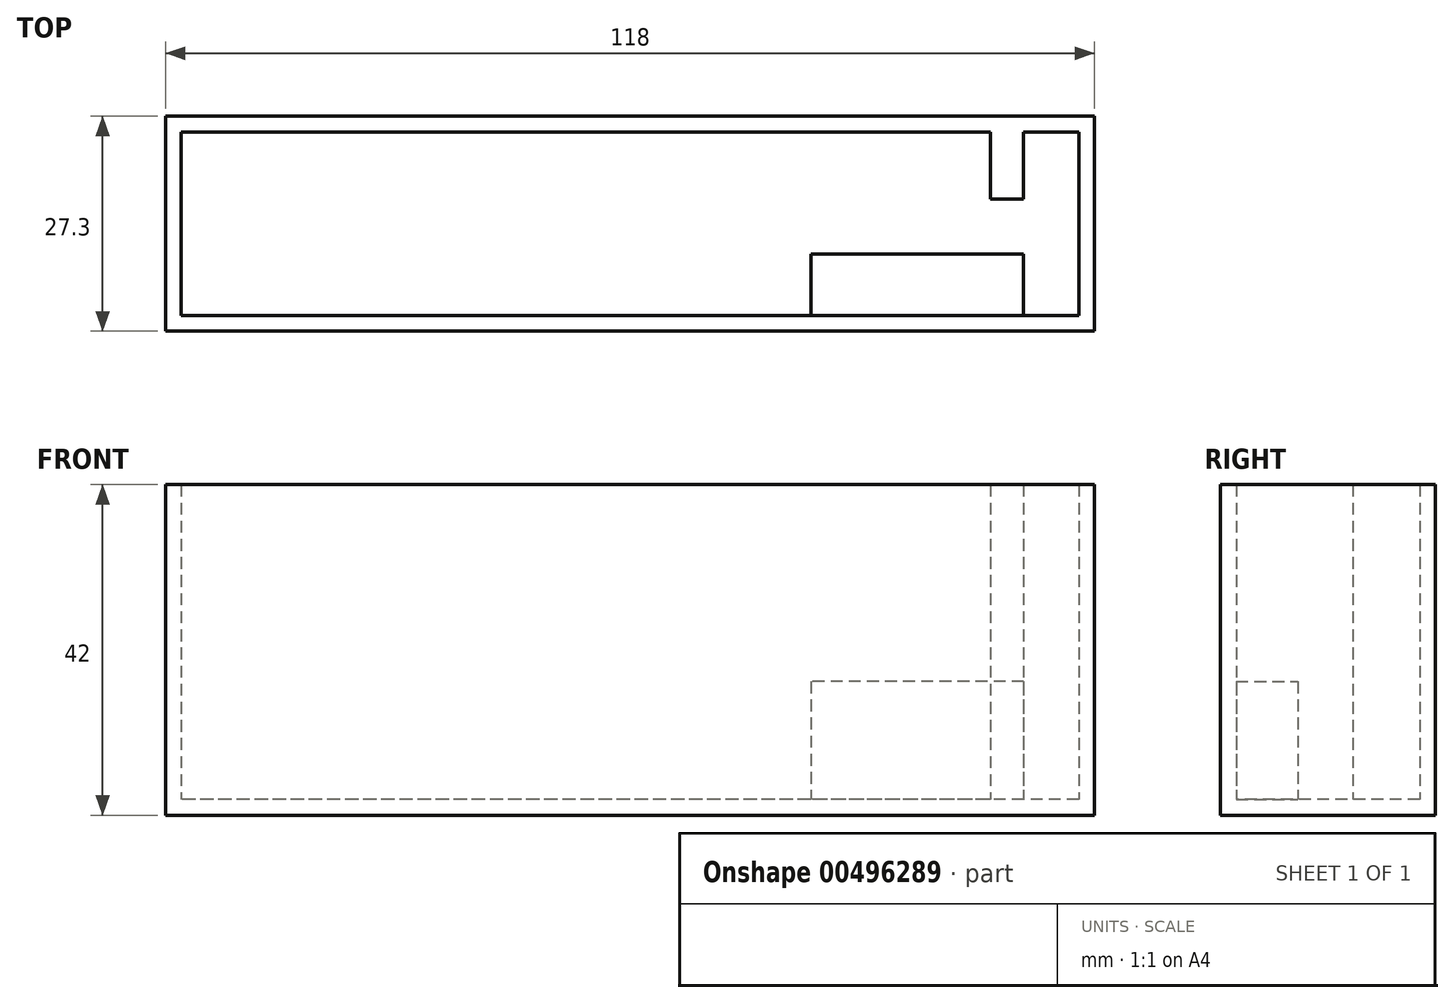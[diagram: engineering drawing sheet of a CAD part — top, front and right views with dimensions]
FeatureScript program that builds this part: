
annotation { "Feature Type Name" : "Feature", "Feature Type Description" : "" }
export const myFeature = defineFeature(function(context is Context, id is Id, definition is map)
    precondition{}
    {
        {
            var Q0;
            Q0=qCreatedBy(makeId("Top.planeOp"),FACE);
            var sketch = newSketch(context, id + "F0", { "sketchPlane" : qUnion([Q0])});
            skLineSegment(sketch, "E0.bottom", {"start": v(55.77, 11.65) * mm, "end": v(-58.23, 11.65) * mm});
            skLineSegment(sketch, "E0.top", {"start": v(55.77, -11.65) * mm, "end": v(-58.23, -11.65) * mm});
            skLineSegment(sketch, "E0.left", {"start": v(55.77, 11.65) * mm, "end": v(55.77, -11.65) * mm});
            skLineSegment(sketch, "E0.right", {"start": v(-58.23, 11.65) * mm, "end": v(-58.23, -11.65) * mm});
            skPoint(sketch, "E0.middle", {"position": v(-1.23, 0) * mm});
            skLineSegment(sketch, "E1.0", {"start": v(-60.23, 13.65) * mm, "end": v(-60.23, -13.65) * mm});
            skLineSegment(sketch, "E2.0", {"start": v(57.77, 13.65) * mm, "end": v(-60.23, 13.65) * mm});
            skLineSegment(sketch, "E3.0", {"start": v(57.77, -13.65) * mm, "end": v(-60.23, -13.65) * mm});
            skLineSegment(sketch, "E4.0", {"start": v(57.77, 13.65) * mm, "end": v(57.77, -13.65) * mm});
            skSolve(sketch);
        }
        {
            var Q0;
            Q0=qSketchRegion(id+"F0",true);
            extrude(context, id + "F1", {"entities" : qUnion([Q0]), "depth" : 40 * mm});
        }
        {
            var Q0;
            Q0=qCreatedBy(makeId("Top.planeOp"),FACE);
            var sketch = newSketch(context, id + "F2", { "sketchPlane" : qUnion([Q0])});
            skPoint(sketch, "E5.0", {"position": v(48.77, 11.65) * mm});
            skLineSegment(sketch, "E6.0", {"start": v(55.77, 11.65) * mm, "end": v(55.77, -11.65) * mm});
            skLineSegment(sketch, "E7.0", {"start": v(55.77, 11.65) * mm, "end": v(-58.23, 11.65) * mm});
            skLineSegment(sketch, "E8.0", {"start": v(55.77, -11.65) * mm, "end": v(-58.23, -11.65) * mm});
            skLineSegment(sketch, "E9", {"start": v(55.77, 11.65) * mm, "end": v(43.05, 11.65) * mm});
            skLineSegment(sketch, "E10.bottom", {"start": v(48.77, 11.65) * mm, "end": v(44.57, 11.65) * mm});
            skLineSegment(sketch, "E10.top", {"start": v(48.77, 3.15) * mm, "end": v(44.57, 3.15) * mm});
            skLineSegment(sketch, "E10.left", {"start": v(48.77, 11.65) * mm, "end": v(48.77, 3.15) * mm});
            skLineSegment(sketch, "E10.right", {"start": v(44.57, 11.65) * mm, "end": v(44.57, 3.15) * mm});
            skSolve(sketch);
        }
        {
            var Q0;
            Q0=qSketchRegion(id+"F2",true);
            extrude(context, id + "F3", {"entities" : qUnion([Q0]), "operationType" : NewBodyOperationType.ADD, "depth" : 40 * mm});
        }
        {
            var Q0;
            Q0=qCreatedBy(makeId("Top.planeOp"),FACE);
            var sketch = newSketch(context, id + "F4", { "sketchPlane" : qUnion([Q0])});
            skPoint(sketch, "E11.0", {"position": v(48.77, -11.65) * mm});
            skLineSegment(sketch, "E12.0", {"start": v(55.77, -11.65) * mm, "end": v(-58.23, -11.65) * mm});
            skLineSegment(sketch, "E13.0", {"start": v(55.77, 11.65) * mm, "end": v(55.77, -11.65) * mm});
            skLineSegment(sketch, "E14.bottom", {"start": v(48.77, -11.65) * mm, "end": v(21.77, -11.65) * mm});
            skLineSegment(sketch, "E14.top", {"start": v(48.77, -3.85) * mm, "end": v(21.77, -3.85) * mm});
            skLineSegment(sketch, "E14.left", {"start": v(48.77, -11.65) * mm, "end": v(48.77, -3.85) * mm});
            skLineSegment(sketch, "E14.right", {"start": v(21.77, -11.65) * mm, "end": v(21.77, -3.85) * mm});
            skSolve(sketch);
        }
        {
            var Q0;
            Q0=qSketchRegion(id+"F4",true);
            extrude(context, id + "F5", {"entities" : qUnion([Q0]), "operationType" : NewBodyOperationType.ADD, "depth" : 15 * mm});
        }
        {
            var Q0;
            Q0=qCreatedBy(makeId("Top.planeOp"),FACE);
            var sketch = newSketch(context, id + "F6", { "sketchPlane" : qUnion([Q0])});
            skPoint(sketch, "E15.0", {"position": v(-60.23, 13.65) * mm});
            skPoint(sketch, "E16.0", {"position": v(57.77, -13.65) * mm});
            skLineSegment(sketch, "E17.bottom", {"start": v(-60.23, 13.65) * mm, "end": v(57.77, 13.65) * mm});
            skLineSegment(sketch, "E17.top", {"start": v(-60.23, -13.65) * mm, "end": v(57.77, -13.65) * mm});
            skLineSegment(sketch, "E17.left", {"start": v(-60.23, 13.65) * mm, "end": v(-60.23, -13.65) * mm});
            skLineSegment(sketch, "E17.right", {"start": v(57.77, 13.65) * mm, "end": v(57.77, -13.65) * mm});
            skSolve(sketch);
        }
        {
            var Q0;
            Q0=qSketchRegion(id+"F6",true);
            extrude(context, id + "F7", {"entities" : qUnion([Q0]), "operationType" : NewBodyOperationType.ADD, "depth" : -2 * mm});
        }
    });
